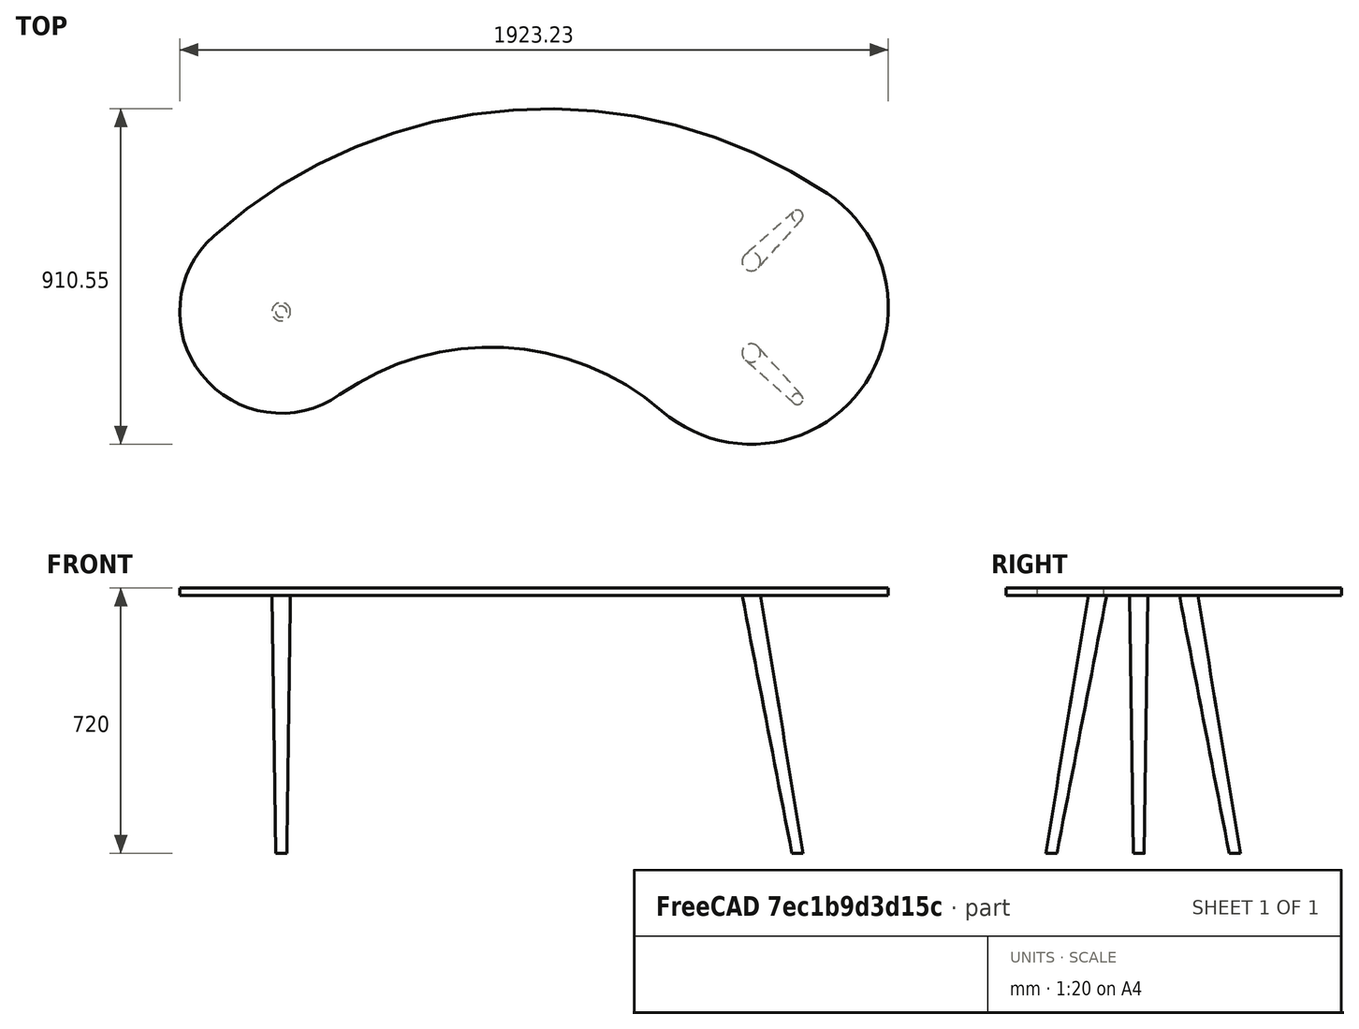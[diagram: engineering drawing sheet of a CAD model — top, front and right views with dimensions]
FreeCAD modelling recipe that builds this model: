
FCSTD DOCUMENT  (FreeCAD 1.0R39319 (Git))
Label: Kidney_Table_FEM
License: All rights reserved
LicenseURL: https://en.wikipedia.org/wiki/All_rights_reserved
objects: Sketcher::SketchObject×8, PartDesign::Body×4, PartDesign::SubShapeBinder×3, PartDesign::AdditiveLoft×3, App::MaterialObjectPython×2, PartDesign::Pad×1, Fem::FemSolverObjectPython×1, App::TextDocument×1, Part::FeaturePython×1, Fem::ConstraintForce×1, Fem::ConstraintFixed×1, Fem::FemAnalysis×1
note: 36 computed .brp shape members not serialized (recipe doc carries the construction recipe); baked Part::Feature solids carry a one-line shape summary decoded from their .brp

FEATURE [Sketcher::SketchObject] Sketch  label="Tabletop Sketch"
  ArcFitTolerance = 1e-06
  AttachmentSupport = -> [XY_Plane]
  FullyConstrained = true
  MakeInternals = false
  MapMode = 5
  sketch-geometry (4):
    g0: ArcOfCircle CenterX=-118.896 CenterY=-603.574 CenterZ=0 NormalX=0 NormalY=0 NormalZ=1 AngleXU=0 Radius=1365.46 StartAngle=0.981973 EndAngle=2.29748
    g1: ArcOfCircle CenterX=-843.06 CenterY=211.04 CenterZ=0 NormalX=0 NormalY=0 NormalZ=1 AngleXU=0 Radius=275.497 StartAngle=2.29748 EndAngle=5.3243
    g2: ArcOfCircle CenterX=-275.43 CenterY=-597.812 CenterZ=0 NormalX=0 NormalY=0 NormalZ=1 AngleXU=0 Radius=712.656 StartAngle=0.858651 EndAngle=2.18271
    g3: ArcOfCircle CenterX=433.08 CenterY=222.92 CenterZ=0 NormalX=0 NormalY=0 NormalZ=1 AngleXU=0 Radius=371.589 StartAngle=4.00024 EndAngle=7.26516
  constraints (12):
    c: Tangent(g3,g0) = -1.5708
    c: Tangent(g3,g2) = 1.5708
    c: Tangent(g2,g1) = 1.5708
    c: Tangent(g1,g0) = -1.5708
    c: Radius(g3) = 371.589
    c: Radius(g1) = 275.497
    c: Radius(g0) = 1365.46
    c: Radius(g2) = 712.656
    c: DistanceY(g-1,g1) = 211.04
    c: DistanceX(g1,g-1) = 843.06
    c: DistanceX(g-1,g3) = 433.08
    c: DistanceY(g-1,g3) = 222.92
FEATURE [PartDesign::Pad] Pad  label="Tabletop Pad"
  Direction = (0,0,1)
  Length = 20
  Length2 = 10
  Profile = -> Sketch
  ReferenceAxis = -> Sketch [N_Axis]
  Refine = true
  Suppressed = false
  Type = 0
FEATURE [PartDesign::Body] Body  label="Tabletop"
  AllowCompound = false
  Group = -> [Pad,Sketch]
  Origin = -> Origin
  Tip = -> Pad
FEATURE [PartDesign::SubShapeBinder] Binder
  BindCopyOnChange = 0
  BindMode = 0
  ClaimChildren = false
  Context = -> Body001 [Binder.]
  Fuse = false
  MakeFace = true
  OffsetFill = false
  OffsetIntersection = false
  OffsetJoinType = 0
  OffsetOpenResult = false
  PartialLoad = false
  Refine = true
  Relative = true
  Support = -> [Pad[Edge6,Edge11]]
  _Version = 2
FEATURE [Sketcher::SketchObject] Sketch001  label="Table Leg 1 Sketch Top"
  ArcFitTolerance = 1e-06
  AttachmentSupport = -> [XY_Plane001]
  ExternalGeometry = -> [Binder]
  FullyConstrained = true
  MakeInternals = false
  MapMode = 5
  sketch-geometry (1):
    g0: Circle CenterX=-843.06 CenterY=211.04 CenterZ=0 NormalX=0 NormalY=0 NormalZ=1 AngleXU=0 Radius=25
  constraints (2):
    c: Coincident(g0,g-3)
    c: Diameter(g0) = 50
FEATURE [Sketcher::SketchObject] Sketch002  label="Table Leg 1 Sketch Bottom"
  ArcFitTolerance = 1e-06
  AttachmentOffset = pos=(0,0,-700) rot=(0,0,1;0rad)
  AttachmentSupport = -> [XY_Plane001]
  ExternalGeometry = -> [Binder]
  FullyConstrained = true
  MakeInternals = false
  MapMode = 5
  Placement = pos=(0,0,-700) rot=(0,0,1;0rad)
  sketch-geometry (1):
    g0: Circle CenterX=-843.06 CenterY=211.04 CenterZ=0 NormalX=0 NormalY=0 NormalZ=1 AngleXU=0 Radius=15
  constraints (2):
    c: Coincident(g0,g-3)
    c: Diameter(g0) = 30
FEATURE [PartDesign::AdditiveLoft] AdditiveLoft  label="Table Leg 1 Additive Loft"
  Closed = true
  Profile = -> Sketch002
  Refine = true
  Ruled = true
  Sections = -> [Sketch001]
  Suppressed = false
FEATURE [PartDesign::Body] Body001  label="Table Leg 1"
  AllowCompound = false
  Group = -> [Binder,Sketch001,Sketch002,AdditiveLoft]
  Origin = -> Origin001
  Tip = -> AdditiveLoft
FEATURE [PartDesign::SubShapeBinder] Binder001
  BindCopyOnChange = 0
  BindMode = 0
  ClaimChildren = false
  Context = -> Body002 [Binder001.]
  Fuse = false
  MakeFace = true
  OffsetFill = false
  OffsetIntersection = false
  OffsetJoinType = 0
  OffsetOpenResult = false
  PartialLoad = false
  Refine = true
  Relative = true
  Support = -> [Pad[Edge6,Edge11]]
  _Version = 2
FEATURE [Sketcher::SketchObject] Sketch003  label="Table Leg 2 Sketch Top"
  ArcFitTolerance = 1e-06
  AttachmentSupport = -> [XY_Plane001]
  ExternalGeometry = -> [Binder001]
  FullyConstrained = false
  MakeInternals = false
  MapMode = 5
  sketch-geometry (2):
    g0: LineSegment [constr] StartX=433.08 StartY=346.783 StartZ=0 EndX=433.08 EndY=594.509 EndZ=0
    g1: Circle CenterX=433.08 CenterY=346.783 CenterZ=0 NormalX=0 NormalY=0 NormalZ=1 AngleXU=0 Radius=25
  constraints (1):
    c: Vertical(g0)
FEATURE [Sketcher::SketchObject] Sketch004  label="Table Leg 2 Sketch Bottom"
  ArcFitTolerance = 1e-06
  AttachmentOffset = pos=(0,0,-700) rot=(0,0,1;0rad)
  AttachmentSupport = -> [XY_Plane001]
  ExternalGeometry = -> [Binder001]
  FullyConstrained = false
  MakeInternals = false
  MapMode = 5
  Placement = pos=(0,0,-700) rot=(0,0,1;0rad)
  sketch-geometry (2):
    g0: LineSegment [constr] StartX=433.08 StartY=346.783 StartZ=0 EndX=433.08 EndY=594.509 EndZ=0
    g1: Circle CenterX=558.08 CenterY=471.783 CenterZ=0 NormalX=0 NormalY=0 NormalZ=1 AngleXU=0 Radius=15
  constraints (3):
    c: Vertical(g0)
    c: DistanceX(g0,g1) = 125
    c: DistanceY(g0,g1) = 125
FEATURE [PartDesign::AdditiveLoft] AdditiveLoft001  label="Table Leg 2 Additive Loft"
  Closed = true
  Profile = -> Sketch004
  Refine = true
  Ruled = true
  Sections = -> [Sketch003]
  Suppressed = false
FEATURE [PartDesign::Body] Body002  label="Table Leg 2"
  AllowCompound = false
  Group = -> [Binder001,Sketch003,Sketch004,AdditiveLoft001]
  Origin = -> Origin002
  Tip = -> AdditiveLoft001
FEATURE [PartDesign::SubShapeBinder] Binder002
  BindCopyOnChange = 0
  BindMode = 0
  ClaimChildren = false
  Context = -> Body003 [Binder002.]
  Fuse = false
  MakeFace = true
  OffsetFill = false
  OffsetIntersection = false
  OffsetJoinType = 0
  OffsetOpenResult = false
  PartialLoad = false
  Refine = true
  Relative = true
  Support = -> [Pad[Edge6,Edge11]]
  _Version = 2
FEATURE [Sketcher::SketchObject] Sketch005  label="Table Leg 3 Sketch Top"
  ArcFitTolerance = 1e-06
  AttachmentSupport = -> [XY_Plane001]
  ExternalGeometry = -> [Binder002]
  FullyConstrained = false
  MakeInternals = false
  MapMode = 5
  sketch-geometry (5):
    g0: Circle [constr] CenterX=433.08 CenterY=222.92 CenterZ=0 NormalX=0 NormalY=0 NormalZ=1 AngleXU=0 Radius=371.589
    g1: LineSegment [constr] StartX=433.08 StartY=-148.669 StartZ=0 EndX=433.08 EndY=99.057 EndZ=0
    g2: LineSegment [constr] StartX=433.08 StartY=99.057 StartZ=0 EndX=433.08 EndY=346.783 EndZ=0
    g3: LineSegment [constr] StartX=433.08 StartY=346.783 StartZ=0 EndX=433.08 EndY=594.509 EndZ=0
    g4: Circle CenterX=433.08 CenterY=99.057 CenterZ=0 NormalX=0 NormalY=0 NormalZ=1 AngleXU=0 Radius=25
  constraints (12):
    c: Coincident(g0,g-4)
    c: PointOnObject(g-4,g0)
    c: PointOnObject(g1,g0)
    c: Coincident(g2,g1)
    c: PointOnObject(g3,g0)
    c: Vertical(g3)
    c: Vertical(g2)
    c: Vertical(g1)
    c: PointOnObject(g0,g2)
    c: Equal(g1,g2)
    c: Equal(g2,g3)
    c: Coincident(g4,g1)
FEATURE [Sketcher::SketchObject] Sketch006  label="Table Leg 3 Sketch Bottom"
  ArcFitTolerance = 1e-06
  AttachmentOffset = pos=(0,0,-700) rot=(0,0,1;0rad)
  AttachmentSupport = -> [XY_Plane001]
  ExternalGeometry = -> [Binder002]
  FullyConstrained = false
  MakeInternals = false
  MapMode = 5
  Placement = pos=(0,0,-700) rot=(0,0,1;0rad)
  sketch-geometry (5):
    g0: Circle [constr] CenterX=433.08 CenterY=222.92 CenterZ=0 NormalX=0 NormalY=0 NormalZ=1 AngleXU=0 Radius=371.589
    g1: LineSegment [constr] StartX=433.08 StartY=-148.669 StartZ=0 EndX=433.08 EndY=99.057 EndZ=0
    g2: LineSegment [constr] StartX=433.08 StartY=99.057 StartZ=0 EndX=433.08 EndY=346.783 EndZ=0
    g3: LineSegment [constr] StartX=433.08 StartY=346.783 StartZ=0 EndX=433.08 EndY=594.509 EndZ=0
    g4: Circle CenterX=558.08 CenterY=-25.943 CenterZ=0 NormalX=0 NormalY=0 NormalZ=1 AngleXU=0 Radius=15
  constraints (13):
    c: Coincident(g0,g-4)
    c: PointOnObject(g-4,g0)
    c: PointOnObject(g1,g0)
    c: Coincident(g2,g1)
    c: PointOnObject(g3,g0)
    c: Vertical(g3)
    c: Vertical(g2)
    c: Vertical(g1)
    c: PointOnObject(g0,g2)
    c: Equal(g1,g2)
    c: Equal(g2,g3)
    c: DistanceX(g1,g4) = 125
    c: DistanceY(g4,g1) = 125
FEATURE [PartDesign::AdditiveLoft] AdditiveLoft002  label="Table Leg 3 Additive Loft"
  Closed = true
  Profile = -> Sketch006
  Refine = true
  Ruled = true
  Sections = -> [Sketch005]
  Suppressed = false
FEATURE [PartDesign::Body] Body003  label="Table Leg 3"
  AllowCompound = false
  Group = -> [Binder002,Sketch005,Sketch006,AdditiveLoft002]
  Origin = -> Origin003
  Tip = -> AdditiveLoft002
FEATURE [Fem::FemSolverObjectPython] SolverCcxTools  # FEM object (typed FeaturePython)
  AnalysisType = 0
  BeamReducedIntegration = true
  BeamShellResultOutput3D = true
  BucklingFactors = 1
  EigenmodeHighLimit = 1000000
  EigenmodeLowLimit = 0
  EigenmodesCount = 10
  GeometricalNonlinearity = 0
  IterationsControlParameterCutb = 0.25,0.5,0.75,0.85,,,1.5,
  IterationsControlParameterIter = 4,8,9,200,10,400,,200,,
  IterationsControlParameterTimeUse = false
  IterationsMaximum = 2000
  IterationsUserDefinedIncrementations = false
  IterationsUserDefinedTimeStepLength = false
  MaterialNonlinearity = 0
  MatrixSolverType = 0
  ModelSpace = 0
  OutputFrequency = 1
  SplitInputWriter = false
  ThermoMechSteadyState = true
  ThermoMechType = 0
  TimeEnd = 1
  TimeInitialStep = 0.01
  TimeMaximumStep = 1
  TimeMinimumStep = 1e-05
FEATURE [App::MaterialObjectPython] MaterialSolid  label="Wood"  # material (typed FeaturePython)
  Category = 0
  Material = AmbientColor=(0.375, 0.1875, 0.0000, 1.0),Author=Bernd Hahnebach,AuthorAndLicense=CC-BY-3.0,CardName=Wood-Generic,Density=7e-07 kg/mm^3,+12 more (map truncated)
  References = -> [Pad]
  UUID = b588224e-e8d6-47ad-ba1f-a058333fd1c6
FEATURE [Sketcher::SketchObject] Sketch008  label="Force Effect Sketch"
  ArcFitTolerance = 1e-06
  AttachmentSupport = -> [Pad]
  FullyConstrained = false
  MakeInternals = false
  MapMode = 5
  Placement = pos=(0,0,20) rot=(0,0,1;0rad)
  sketch-geometry (4):
    g0: LineSegment StartX=-238.103 StartY=703.208 StartZ=0 EndX=-238.103 EndY=574.833 EndZ=0
    g1: LineSegment StartX=-238.103 StartY=574.833 StartZ=0 EndX=-94.6256 EndY=574.833 EndZ=0
    g2: LineSegment StartX=-94.6256 StartY=574.833 StartZ=0 EndX=-94.6256 EndY=703.208 EndZ=0
    g3: LineSegment StartX=-94.6256 StartY=703.208 StartZ=0 EndX=-238.103 EndY=703.208 EndZ=0
  constraints (8):
    c: Coincident(g0,g1)
    c: Coincident(g1,g2)
    c: Coincident(g2,g3)
    c: Coincident(g3,g0)
    c: Vertical(g0)
    c: Vertical(g2)
    c: Horizontal(g1)
    c: Horizontal(g3)
FEATURE [App::TextDocument] Text_document  label="README"
  Text = An error message appears when writing the .inp file in the Solver if the Force Effect Sketch is an ellipse.
FEATURE [App::MaterialObjectPython] MaterialSolid001  label="Aluminium"  # material (typed FeaturePython)
  Category = 0
  Material = AmbientColor=(0.3000, 0.3000, 0.3000, 1.0),Author=Uwe Stöhr,CardName=Aluminum-Generic,Density=2.7e-06 kg/mm^3,+17 more (map truncated)
  References = -> [AdditiveLoft002,AdditiveLoft001,AdditiveLoft]
  UUID = 9bf060e9-1663-44a2-88e2-2ff6ee858efe
FEATURE [Part::FeaturePython] BooleanFragments  label="Table"  # WARN: FeaturePython — macro-defined, semantics opaque (R4)
  Mode = 0
  Objects = -> [Body,Body001,Body002,Body003,Sketch008]
  Tolerance = 0
FEATURE [Fem::ConstraintForce] ConstraintForce
  DirectionVector = (0,0,-1)
  Force = 1000000
  NormalDirection = (0,0,1)
  Normals = (16) [(0,0,1),(0,0,1),(0,0,1),(0,0,1),(0,0,1),(0,0,1),(0,0,1),(0,0,1),(0,0,1),(0,0,1),(0,0,1),(0,0,1),(0,0,1),(0,0,1),(0,0,1),(0,0,1)]
  Points = (16) [(-238.103,574.833,20),(-190.277,574.833,20),(-142.452,574.833,20),(-94.6256,574.833,20),(-238.103,617.625,20),(-190.277,617.625,20),+10 more]
  References = -> [BooleanFragments]
  Reversed = true
  Suppressed = false
FEATURE [Fem::ConstraintFixed] ConstraintFixed
  NormalDirection = (0,0,-1)
  Normals = (12) [(0,0,-1),(0,0,-1),(0,0,-1),(0,0,-1),(0,0,-1),(0,0,-1),(0,0,-1),(0,0,-1),(0,0,-1),(0,0,-1),(0,0,-1),(0,0,-1)]
  Points = (12) [(-848.06,206.04,-700),(-838.06,206.04,-700),(-848.06,216.04,-700),(-838.06,216.04,-700),(553.08,466.783,-700),(563.08,466.783,-700),+6 more]
  References = -> [AdditiveLoft,AdditiveLoft001,AdditiveLoft002]
  Suppressed = false
FEATURE [Fem::FemAnalysis] Analysis
  Group = -> [SolverCcxTools,MaterialSolid,MaterialSolid001,ConstraintForce,ConstraintFixed]
